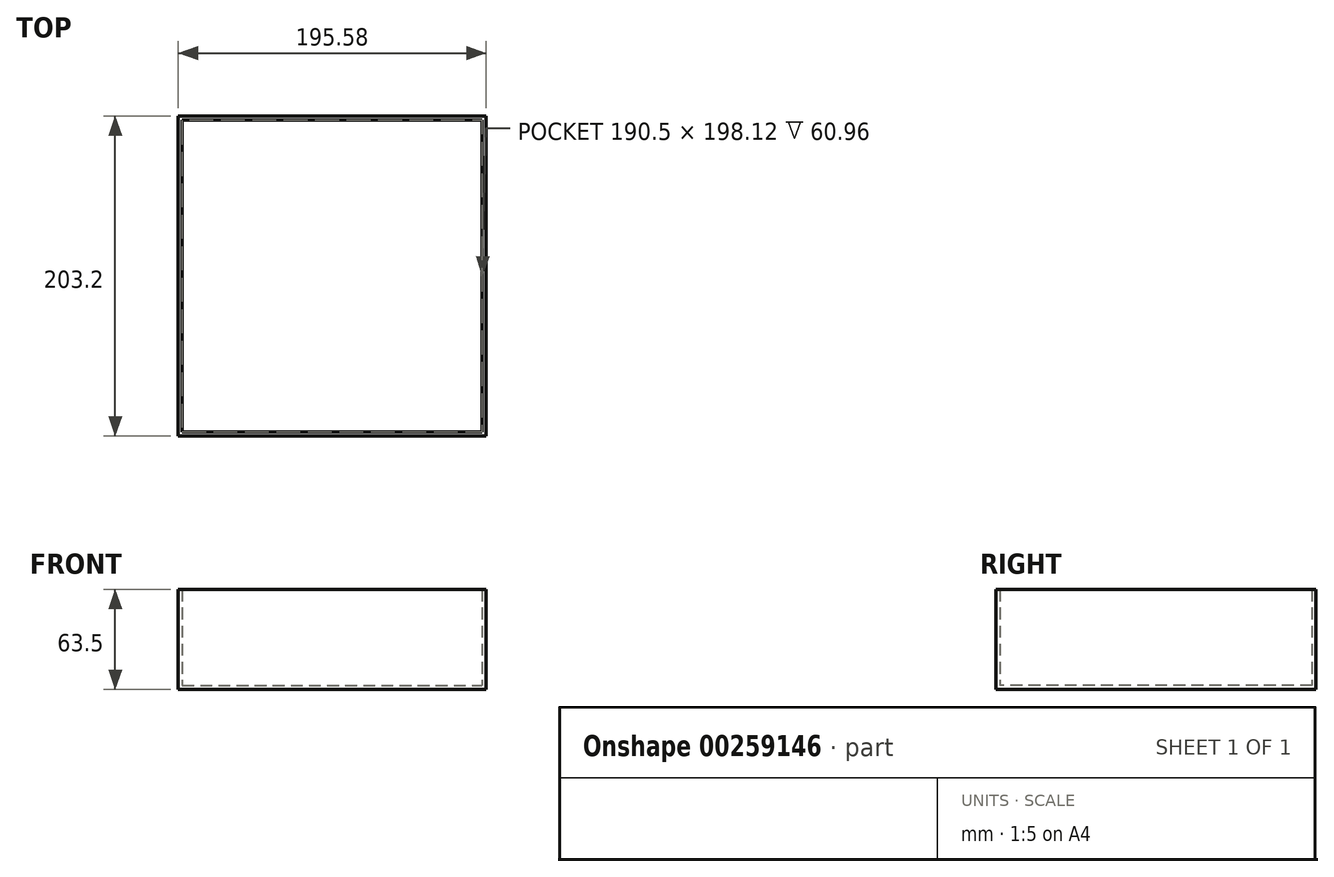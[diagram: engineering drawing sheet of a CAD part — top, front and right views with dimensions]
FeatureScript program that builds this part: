
annotation { "Feature Type Name" : "Feature", "Feature Type Description" : "" }
export const myFeature = defineFeature(function(context is Context, id is Id, definition is map)
    precondition{}
    {
        {
            var Q0;
            Q0=qCreatedBy(makeId("Top.planeOp"),FACE);
            var sketch = newSketch(context, id + "F0", { "sketchPlane" : qUnion([Q0])});
            skLineSegment(sketch, "E0", {"start": v(0, 0) * mm, "end": v(0, 101.6) * mm});
            skLineSegment(sketch, "E1", {"start": v(0, 101.6) * mm, "end": v(97.8, 101.6) * mm});
            skLineSegment(sketch, "E2", {"start": v(97.8, 101.6) * mm, "end": v(97.8, 0) * mm});
            skLineSegment(sketch, "E3.MirrorCS", {"start": v(0, 101.6) * mm, "end": v(-97.8, 101.6) * mm});
            skLineSegment(sketch, "E4.MirrorCS", {"start": v(97.8, -101.6) * mm, "end": v(97.79, 0) * mm});
            skLineSegment(sketch, "E5", {"start": v(-97.8, -101.6) * mm, "end": v(97.8, -101.6) * mm});
            skLineSegment(sketch, "E6", {"start": v(-97.8, 101.6) * mm, "end": v(-97.8, -101.6) * mm});
            skSolve(sketch);
        }
        {
            var Q0;
            Q0 = qSketchRegion(id + "F0", true);
            extrude(context, id + "F1", {"entities" : qUnion([Q0]), "depth" : 63.5 * mm});
        }
        {
            var Q0;
            Q0=makeQuery(id+"F1.opExtrude","CAP_FACE",FACE,{"disambiguationData":[OSD([sQuery(id+"F0.wireOp",EDGE,"E1"),sQuery(id+"F0.wireOp",EDGE,"E2"),sQuery(id+"F0.wireOp",EDGE,"E3.MirrorCS"),sQuery(id+"F0.wireOp",EDGE,"E4.MirrorCS"),sQuery(id+"F0.wireOp",EDGE,"E5"),sQuery(id+"F0.wireOp",EDGE,"E6")])],"isStart":false});
            shell(context, id + "F2", {"entities" : qUnion([Q0]), "thickness" : 2.54 * mm});
        }
    });
